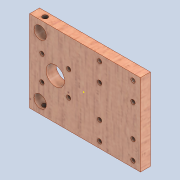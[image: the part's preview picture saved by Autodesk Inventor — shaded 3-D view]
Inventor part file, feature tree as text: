
AUTODESK INVENTOR PART (.ipt)
format: ipt  version: 2020 (Build 240168000, 168)  size: 214,016 bytes
history: native  units: mm
features: sketch x7, other x6, extrude x4, hole x3, pattern_linear x2, reference x2, direct_edit x1, move_body x1
ambient origin geometry x8: Origin, YZ Plane, XZ Plane, XY Plane, X Axis, Y Axis, Z Axis, Center Point
bodies: Solid1 (feature_tree)
feature tree (26):
  extrude  "Extrusion1"  Depth=66.0mm
  extrude  "Extrusion4"  TaperAngle=0.0deg  [1 undecoded]
  extrude  "Extrusion5"  TaperAngle=0.0deg  [1 undecoded]
  extrude  "Extrusion6"  Depth=9.0mm
  sketch  "Sketch7"  dims[d27=8.5mm d28=9.0mm]
  hole  "Hole1"  [1 undecoded]
  direct_edit  "Direct Edit1"
  pattern_linear  "Rectangular Pattern2"  Spacing1=3.5mm  [1 undecoded]
  pattern_linear  "Rectangular Pattern3"  Spacing1=21.5mm  [1 undecoded]
  hole  "Hole2"  [1 undecoded]
  hole  "Hole3"  [1 undecoded]
  sketch  "Sketch1"  dims[d0=87.5mm d1=66.0mm]
  sketch  "Sketch4"  dims[d2=8.0mm d3=0.0mm d19=0.0mm d20=0.0mm]
  sketch  "Sketch6"  dims[d24=15.0mm d25=0.0mm d26=0.0mm]
  sketch  "Sketch8"  dims[d29=10.0mm d30=9.0mm]
  reference  "Reference7"
  reference  "Reference8"
  sketch  "Sketch10"  dims[d31=0.0mm d32=0.0mm]
  sketch  "Sketch11"  dims[d33=20.748842mm d35=3.5mm d36=21.5mm d37=20.0mm d38=4.0mm d39=5.0mm d40=15.0mm d41=5.0mm d42=15.0mm d43=3.5mm d44=6.0mm d45=4.0mm d46=2.0mm d47=90.0deg d48=8.0mm d49=20.594885mm d53=0.0mm d54=0.0mm d55=2.0mm d56=26.0mm d57=20.0mm d59=15.0mm d60=20.0mm d62=41.0mm d63=20.0mm d65=27.0mm d66=8.5mm d67=4.134mm d68=5.0mm d69=4.0mm d70=2.0mm d71=90.0deg d72=7.45mm d73=20.594885mm d74=8.5mm d75=4.134mm d76=5.0mm d77=4.0mm d78=2.0mm d79=90.0deg d80=7.45mm d81=20.594885mm]
  parser-record x1  (decoder bookkeeping rows leaked as tree rows — omitted from the tree; the rows remain in map.json)
  other  "0005-00-00 Ansamblu_General.iam"
  other  "Surub M4 saiba piulita.iam:65"
  other  "0005-10-1013 ISO 7089 - 4 - 140 HV.ipt:2"
  move_body  "Move1"
  other  "0005-10-04 Z axis and extruder.iam"
  other  "0005-10-1002  Hub.ipt:22"
note: 7 required parameter values undecoded (feature->parameter linkage not recoverable at this tier; creation-order binding heuristic only, values carry confidence <= 0.55)
note: 1 file-system path scrubbed to <path> (originals preserved in map.json)
